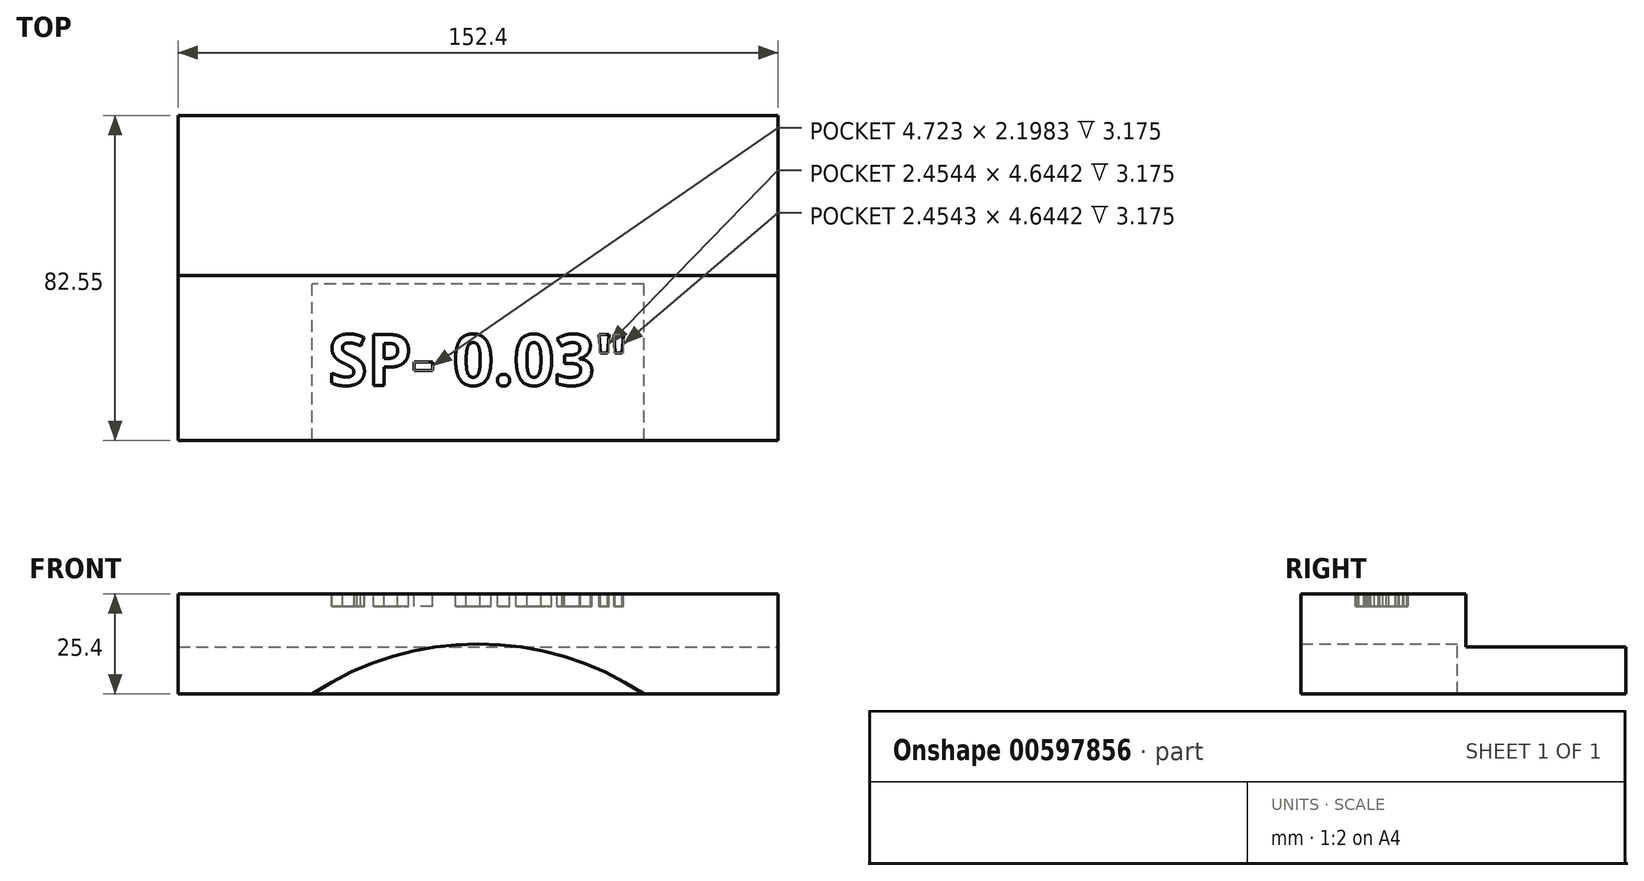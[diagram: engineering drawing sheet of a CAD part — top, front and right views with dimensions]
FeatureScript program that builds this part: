
annotation { "Feature Type Name" : "Feature", "Feature Type Description" : "" }
export const myFeature = defineFeature(function(context is Context, id is Id, definition is map)
    precondition{}
    {
        {
            var Q0;
            Q0=qCreatedBy(makeId("Front.planeOp"),FACE);
            var sketch = newSketch(context, id + "F0", { "sketchPlane" : qUnion([Q0])});
            skLineSegment(sketch, "E0.bottom", {"start": v(0, 0) * mm, "end": v(34.08, 0) * mm});
            skLineSegment(sketch, "E0.top", {"start": v(0, 25.4) * mm, "end": v(152.4, 25.4) * mm});
            skLineSegment(sketch, "E0.left", {"start": v(0, 0) * mm, "end": v(0, 25.4) * mm});
            skLineSegment(sketch, "E0.right", {"start": v(152.4, 0) * mm, "end": v(152.4, 25.4) * mm});
            skArc(sketch, "E1", {"start": v(118.32, 0) * mm, "mid": v(76.2, 12.7) * mm, "end": v(34.08, 0) * mm});
            skPoint(sketch, "E1.centerSnap0", {"position": v(76.2, 0) * mm});
            skLineSegment(sketch, "E2.trimOffspring", {"start": v(118.32, 0) * mm, "end": v(152.4, 0) * mm});
            skLineSegment(sketch, "E3", {"start": v(152.4, 12.7) * mm, "end": v(0, 12.7) * mm, "construction": true});
            skSolve(sketch);
        }
        {
            var Q0;
            Q0=qSketchRegion(id+"F0",true);
            extrude(context, id + "F1", {"entities" : qUnion([Q0]), "depth" : 39.69 * mm, "offsetDistance" : 25.4 * mm});
        }
        {
            var Q0;
            Q0=makeQuery(id+"F1.opExtrude","CAP_FACE",FACE,{"disambiguationData":[OSD([sQuery(id+"F0.wireOp",EDGE,"E0.bottom"),sQuery(id+"F0.wireOp",EDGE,"E0.top"),sQuery(id+"F0.wireOp",EDGE,"E0.left"),sQuery(id+"F0.wireOp",EDGE,"E0.right"),sQuery(id+"F0.wireOp",EDGE,"E1"),sQuery(id+"F0.wireOp",EDGE,"E2.trimOffspring")])],"isStart":true});
            var sketch = newSketch(context, id + "F2", { "sketchPlane" : qUnion([Q0])});
            skLineSegment(sketch, "E4.bottom", {"start": v(-152.4, 0) * mm, "end": v(0, 0) * mm});
            skLineSegment(sketch, "E4.top", {"start": v(-152.4, 25.4) * mm, "end": v(0, 25.4) * mm});
            skLineSegment(sketch, "E4.left", {"start": v(-152.4, 0) * mm, "end": v(-152.4, 25.4) * mm});
            skLineSegment(sketch, "E4.right", {"start": v(0, 0) * mm, "end": v(0, 25.4) * mm});
            skSolve(sketch);
        }
        {
            var Q0;
            Q0=qSketchRegion(id+"F2",true);
            extrude(context, id + "F3", {"entities" : qUnion([Q0]), "operationType" : NewBodyOperationType.ADD, "depth" : 42.86 * mm, "offsetDistance" : 25.4 * mm});
        }
        {
            var Q0;
            Q0=makeQuery(id+"F3.opExtrude","CAP_FACE",FACE,{"disambiguationData":[OSD([sQuery(id+"F2.wireOp",EDGE,"E4.bottom"),sQuery(id+"F2.wireOp",EDGE,"E4.top"),sQuery(id+"F2.wireOp",EDGE,"E4.left"),sQuery(id+"F2.wireOp",EDGE,"E4.right")])],"isStart":false});
            var sketch = newSketch(context, id + "F4", { "sketchPlane" : qUnion([Q0])});
            skLineSegment(sketch, "E5.bottom", {"start": v(0, 25.4) * mm, "end": v(-152.4, 25.4) * mm});
            skLineSegment(sketch, "E5.top", {"start": v(0, 11.94) * mm, "end": v(-152.4, 11.94) * mm});
            skLineSegment(sketch, "E5.left", {"start": v(0, 25.4) * mm, "end": v(0, 11.94) * mm});
            skLineSegment(sketch, "E5.right", {"start": v(-152.4, 25.4) * mm, "end": v(-152.4, 11.94) * mm});
            skSolve(sketch);
        }
        {
            var Q0;
            Q0=qSketchRegion(id+"F4",true);
            extrude(context, id + "F5", {"entities" : qUnion([Q0]), "operationType" : NewBodyOperationType.REMOVE, "oppositeDirection" : true, "depth" : 40.64 * mm, "offsetDistance" : 25.4 * mm});
        }
        {
            var Q0;
            Q0=makeQuery(id+"F3.boolean.opBoolean","MERGE",FACE,{"derivedFrom":[makeQuery(id+"F1.opExtrude","SWEPT_FACE",FACE,{"disambiguationData":[OSD([sQuery(id+"F0.wireOp",EDGE,"E0.top")])]}),makeQuery(id+"F3.opExtrude","SWEPT_FACE",FACE,{"disambiguationData":[OSD([sQuery(id+"F2.wireOp",EDGE,"E4.top")])]})]});
            var sketch = newSketch(context, id + "F6", { "sketchPlane" : qUnion([Q0])});
            skText(sketch, "E6", { "text": "SP- 0.03\"", "fontName": "OpenSans-Bold.ttf"});
            const initialGuessF6  = {"E6": [0.0381, -0.02566, 1, 0, 0.01297]};
            skSetInitialGuess(sketch, initialGuessF6);
            skSolve(sketch);
        }
        {
            var Q0;
            Q0 = qSketchRegion(id + "F6", true);
            extrude(context, id + "F7", {"entities" : qUnion([Q0]), "operationType" : NewBodyOperationType.REMOVE, "oppositeDirection" : true, "depth" : 3.17 * mm, "offsetDistance" : 25.4 * mm});
        }
    });
